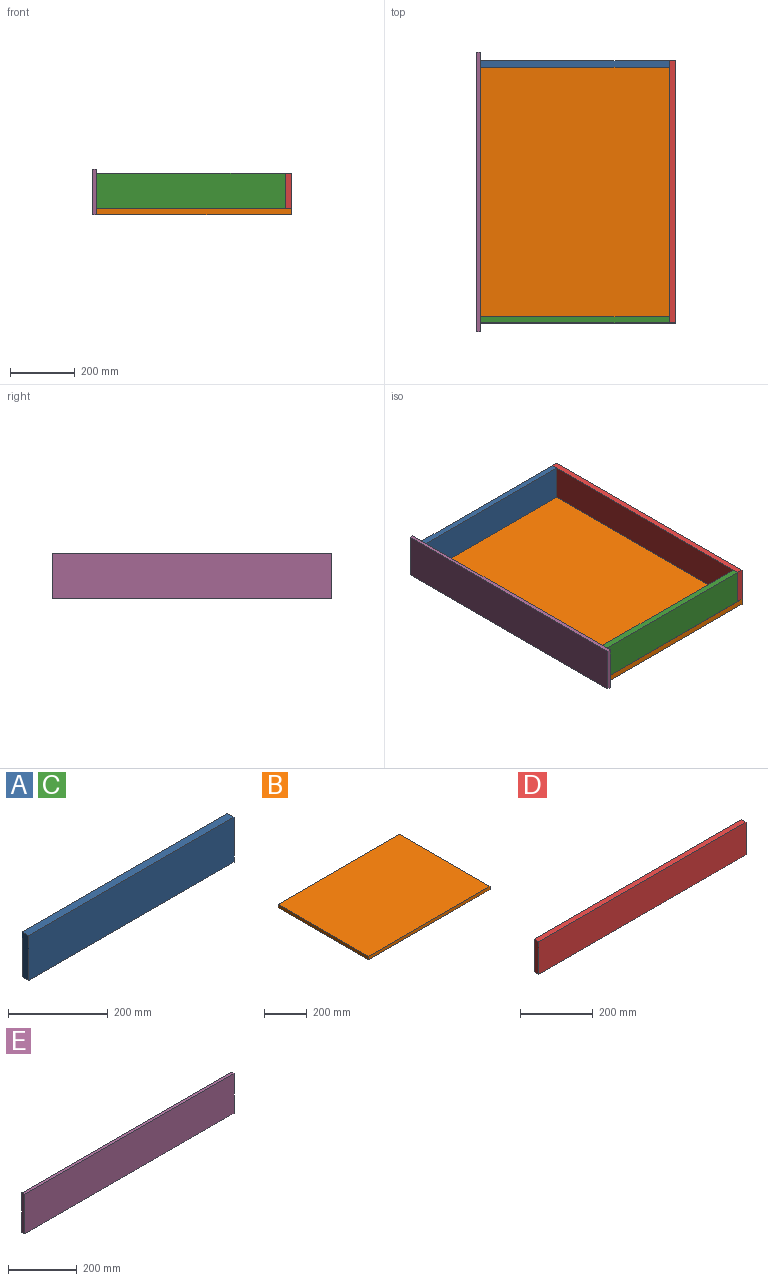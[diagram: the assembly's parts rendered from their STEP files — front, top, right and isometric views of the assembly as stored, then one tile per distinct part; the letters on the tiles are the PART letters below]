
ASSEMBLY  parts=5 mates=4
PART A: 6 faces, bbox 581x19x110 mm
  f0: plane 110x19mm, normal (-1,0,0), area 2090mm2, adj f1,f3,f4,f5
  f1: plane 581x19mm, normal (0,0,-1), area 11039mm2, adj f0,f2,f4,f5
  f2: plane 110x19mm, normal (1,0,0), area 2090mm2, adj f1,f3,f4,f5
  f3: plane 581x19mm, normal (0,0,1), area 11039mm2, adj f0,f2,f4,f5
  f4: plane 581x110mm, normal (0,-1,0), area 63910mm2, adj f0,f1,f2,f3
  f5: plane 581x110mm, normal (0,1,0), area 63910mm2, adj f0,f1,f2,f3
PART B: 6 faces, bbox 807x600x19 mm
  f0: plane 600x19mm, normal (-1,0,0), area 11400mm2, adj f1,f3,f4,f5
  f1: plane 807x19mm, normal (0,-1,0), area 15333mm2, adj f0,f2,f4,f5
  f2: plane 600x19mm, normal (1,0,0), area 11400mm2, adj f1,f3,f4,f5
  f3: plane 807x19mm, normal (0,1,0), area 15333mm2, adj f0,f2,f4,f5
  f4: plane 807x600mm, normal (0,0,1), area 484200mm2, adj f0,f1,f2,f3
  f5: plane 807x600mm, normal (0,0,-1), area 484200mm2, adj f0,f1,f2,f3
PART C: same geometry as A
PART D: 6 faces, bbox 807x19x110 mm
  f0: plane 110x19mm, normal (-1,0,0), area 2090mm2, adj f1,f3,f4,f5
  f1: plane 807x19mm, normal (0,0,-1), area 15333mm2, adj f0,f2,f4,f5
  f2: plane 110x19mm, normal (1,0,0), area 2090mm2, adj f1,f3,f4,f5
  f3: plane 807x19mm, normal (0,0,1), area 15333mm2, adj f0,f2,f4,f5
  f4: plane 807x110mm, normal (0,-1,0), area 88770mm2, adj f0,f1,f2,f3
  f5: plane 807x110mm, normal (0,1,0), area 88770mm2, adj f0,f1,f2,f3
PART E: 6 faces, bbox 861x12x141 mm
  f0: plane 861x12mm, normal (0,0,1), area 10332mm2, adj f1,f3,f4,f5
  f1: plane 141x12mm, normal (-1,0,0), area 1692mm2, adj f0,f2,f4,f5
  f2: plane 861x12mm, normal (0,0,-1), area 10332mm2, adj f1,f3,f4,f5
  f3: plane 141x12mm, normal (1,0,0), area 1692mm2, adj f0,f2,f4,f5
  f4: plane 861x141mm, normal (0,-1,0), area 121401mm2, adj f0,f1,f2,f3
  f5: plane 861x141mm, normal (0,1,0), area 121401mm2, adj f0,f1,f2,f3
PLACE A t=(40.43,490.24,29.19)mm
PLACE B rot(axis=(0,0,-1),90deg) t=(40.43,490.24,10.19)mm
PLACE C t=(40.43,-297.76,29.19)mm
PLACE D rot(axis=(0,0,1),90deg) t=(621.43,-316.76,29.19)mm
PLACE E rot(axis=(0,0,-1),90deg) t=(40.43,86.74,80.69)mm
MATE fastened B.f4 <-> D.f1  axis (0,0,1) through (640.43,86.74,29.19)mm
MATE fastened C.f2 <-> D.f5  axis (1,0,0) through (621.43,-316.76,29.19)mm
MATE fastened B.f1 <-> E.f5  axis (-1,0,0) through (40.43,86.74,10.19)mm
MATE fastened D.f5 <-> A.f2  axis (-1,0,0) through (621.43,490.24,29.19)mm
